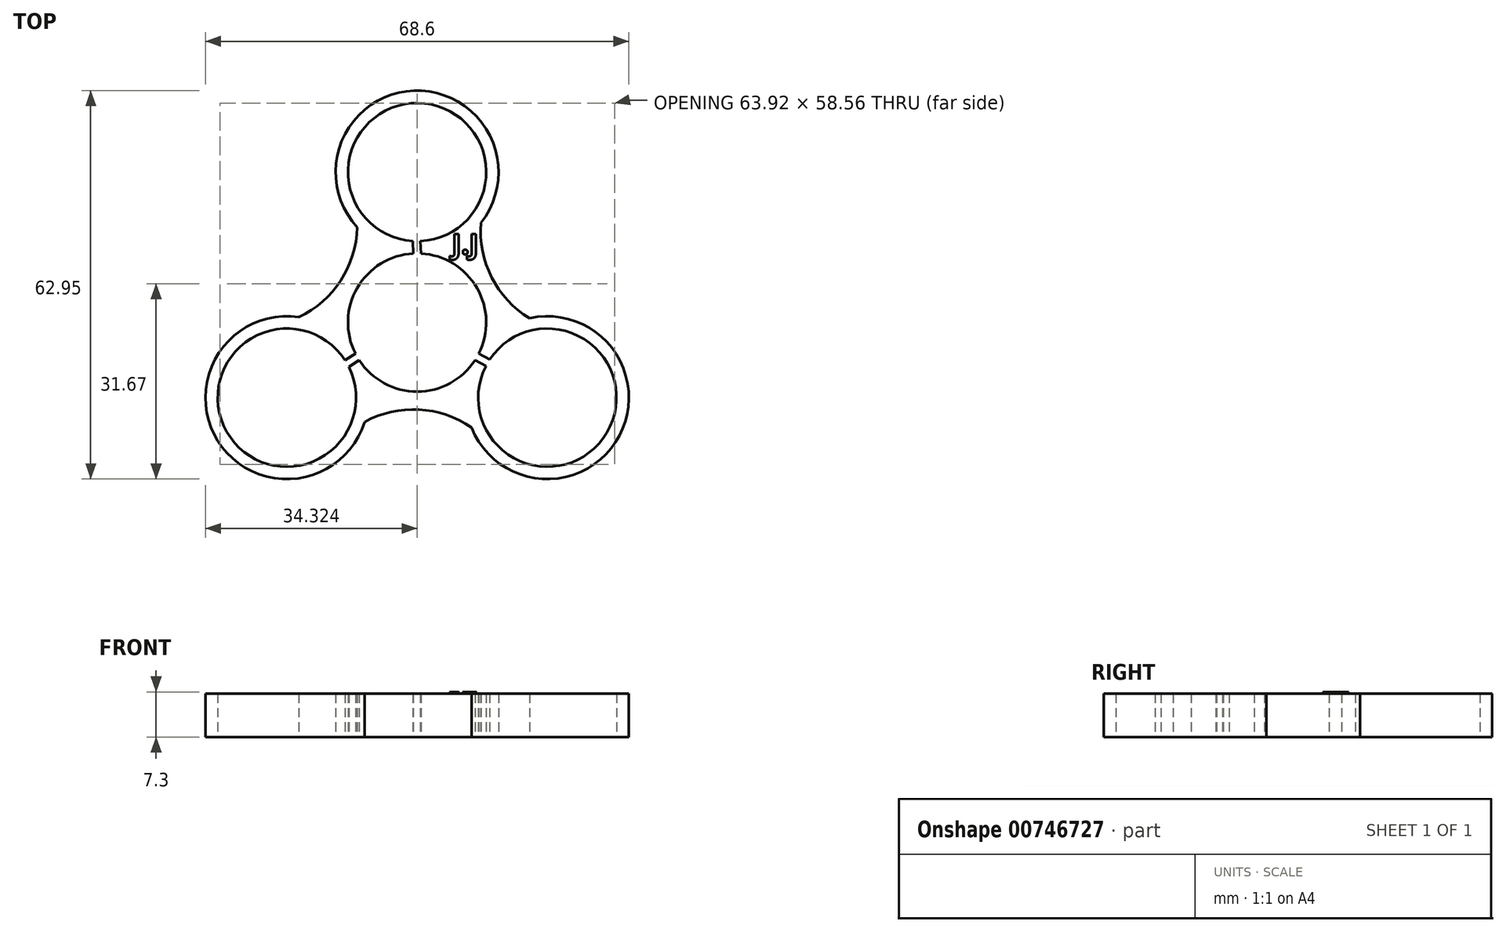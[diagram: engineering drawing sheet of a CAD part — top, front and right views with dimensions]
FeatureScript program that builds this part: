
annotation { "Feature Type Name" : "Feature", "Feature Type Description" : "" }
export const myFeature = defineFeature(function(context is Context, id is Id, definition is map)
    precondition{}
    {
        {
            var Q0;
            Q0=qCreatedBy(makeId("Top.planeOp"),FACE);
            var sketch = newSketch(context, id + "F0", { "sketchPlane" : qUnion([Q0])});
            skCircle(sketch, "E0", {"center": v(0, 0) * mm, "radius": 11.2 * mm});
            skArc(sketch, "E1", {"start": v(10.34, 16.16) * mm, "mid": v(-0.49, 37.56) * mm, "end": v(-9.7, 15.42) * mm});
            skCircle(sketch, "E2", {"center": v(0, 24.37) * mm, "radius": 11.2 * mm});
            skArc(sketch, "E3.1.0", {"start": v(-19.17, 0.87) * mm, "mid": v(-32.28, -19.2) * mm, "end": v(-8.5, -16.12) * mm});
            skArc(sketch, "E3.2.0", {"start": v(10, -5.06) * mm, "mid": v(9.67, -5.58) * mm, "end": v(9.38, -6.12) * mm});
            skCircle(sketch, "E4.1.0", {"center": v(-21.1, -12.18) * mm, "radius": 11.2 * mm});
            skCircle(sketch, "E4.2.0", {"center": v(21.1, -12.18) * mm, "radius": 11.2 * mm});
            skArc(sketch, "E5", {"start": v(10.34, 16.16) * mm, "mid": v(12.08, 7.31) * mm, "end": v(18.2, 0.7) * mm});
            skArc(sketch, "E6.1.0", {"start": v(-19.17, 0.87) * mm, "mid": v(-12.37, 6.8) * mm, "end": v(-9.7, 15.42) * mm});
            skArc(sketch, "E6.2.0", {"start": v(8.83, -17.04) * mm, "mid": v(0.3, -14.12) * mm, "end": v(-8.5, -16.12) * mm});
            skArc(sketch, "E7.trimOffspring", {"start": v(8.83, -17.04) * mm, "mid": v(32.77, -18.36) * mm, "end": v(18.2, 0.7) * mm});
            skArc(sketch, "E8.trimOffspring", {"start": v(-9.38, -6.12) * mm, "mid": v(-9.67, -5.58) * mm, "end": v(-10, -5.06) * mm});
            skArc(sketch, "E9.trimOffspring", {"start": v(-0.61, 11.18) * mm, "mid": v(0, 11.17) * mm, "end": v(0.61, 11.18) * mm});
            skLineSegment(sketch, "E10", {"start": v(9.38, -6.12) * mm, "end": v(11.15, -7.05) * mm});
            skLineSegment(sketch, "E11", {"start": v(10, -5.06) * mm, "end": v(11.78, -5.97) * mm});
            skLineSegment(sketch, "E12.1.0", {"start": v(-0.61, 11.18) * mm, "end": v(-0.72, 13.2) * mm});
            skLineSegment(sketch, "E12.2.0", {"start": v(-9.38, -6.12) * mm, "end": v(-11.07, -7.22) * mm});
            skLineSegment(sketch, "E13.1.0", {"start": v(0.61, 11.18) * mm, "end": v(0.53, 13.18) * mm});
            skLineSegment(sketch, "E13.2.0", {"start": v(-10, -5.06) * mm, "end": v(-11.68, -6.14) * mm});
            skSolve(sketch);
        }
        {
            var Q0;
            Q0=makeQuery(id+"F0.imprint","IMPRINT",FACE,{"disambiguationData":[TD([[makeQuery(id+"F0.imprint","IMPRINT",EDGE,{"derivedFrom":sQuery(id+"F0.wireOp",EDGE,"E1")}),1.0]])]});
            extrude(context, id + "F1", {"entities" : qUnion([Q0]), "depth" : 7 * mm, "offsetDistance" : 25 * mm});
        }
        {
            var Q0;
            Q0=makeQuery(id+"F1.opExtrude","CAP_FACE",FACE,{"disambiguationData":[OSD([sQuery(id+"F0.wireOp",EDGE,"E0"),sQuery(id+"F0.wireOp",EDGE,"E1"),sQuery(id+"F0.wireOp",EDGE,"E2"),sQuery(id+"F0.wireOp",EDGE,"E3.1.0"),sQuery(id+"F0.wireOp",EDGE,"E4.1.0"),sQuery(id+"F0.wireOp",EDGE,"E4.2.0"),sQuery(id+"F0.wireOp",EDGE,"E5"),sQuery(id+"F0.wireOp",EDGE,"E6.1.0"),sQuery(id+"F0.wireOp",EDGE,"E6.2.0"),sQuery(id+"F0.wireOp",EDGE,"E7.trimOffspring"),sQuery(id+"F0.wireOp",EDGE,"E10"),sQuery(id+"F0.wireOp",EDGE,"E11"),sQuery(id+"F0.wireOp",EDGE,"E12.1.0"),sQuery(id+"F0.wireOp",EDGE,"E12.2.0"),sQuery(id+"F0.wireOp",EDGE,"E13.1.0"),sQuery(id+"F0.wireOp",EDGE,"E13.2.0")])],"isStart":false});
            var sketch = newSketch(context, id + "F2", { "sketchPlane" : qUnion([Q0])});
            skText(sketch, "E14", { "text": "J.J", "fontName": "OpenSans-Bold.ttf"});
            const initialGuessF2  = {"E14": [0.00564, 0.0111, 1, 0, 0.00327]};
            skSetInitialGuess(sketch, initialGuessF2);
            skSolve(sketch);
        }
        {
            var Q0;
            Q0 = qSketchRegion(id + "F2", true);
            extrude(context, id + "F3", {"entities" : qUnion([Q0]), "operationType" : NewBodyOperationType.ADD, "depth" : 0.3 * mm, "offsetDistance" : 25 * mm});
        }
    });
